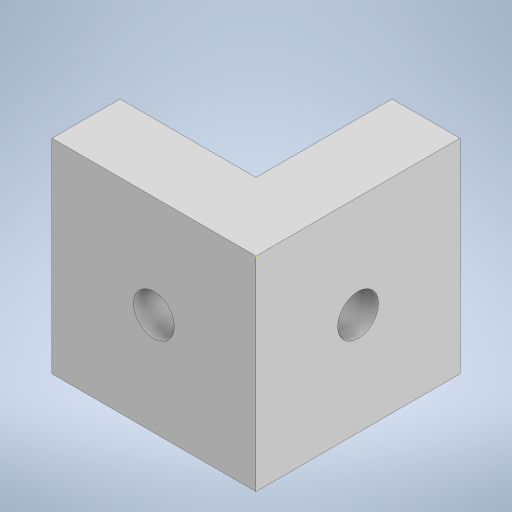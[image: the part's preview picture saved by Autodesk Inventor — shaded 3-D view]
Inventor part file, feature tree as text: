
AUTODESK INVENTOR PART (.ipt)
format: ipt  version: 2023 (Build 270158000, 158)  size: 225,792 bytes
history: native  units: mm
features: sketch x8, extrude x6
ambient origin geometry x8: Origin, YZ Plane, XZ Plane, XY Plane, X Axis, Y Axis, Z Axis, Center Point
bodies: Body1 (feature_tree)
feature tree (14):
  extrude  "Extrusion25"  Depth=30.0mm
  extrude  "Extrusion26"  Depth=30.0mm
  sketch  "Sketch37"  dims[d117=30.0mm d118=10.0mm d119=0.0mm]
  extrude  "Extrusion28"  Depth=10.0mm TaperAngle=0.0deg
  sketch  "Sketch39"  dims[d135=9.0mm d136=5.0mm d137=0.0mm]
  extrude  "Extrusion32"  Depth=10.0mm TaperAngle=0.0deg
  extrude  "Extrusion33"  Depth=5.0mm TaperAngle=0.0deg
  extrude  "Extrusion34"  Depth=5.0mm TaperAngle=0.0deg
  sketch  "Sketch34"  dims[d112=30.0mm d113=30.0mm]
  sketch  "Sketch35"  dims[d114=10.0mm d115=0.0mm d116=30.0mm]
  sketch  "Sketch38"  dims[d123=6.0mm d124=10.0mm d125=0.0mm]
  sketch  "Sketch43"  dims[d138=9.0mm d139=5.0mm d140=0.0mm]
  sketch  "Sketch44"  dims[d141=6.0mm]
  sketch  "Sketch45"  dims[d142=10.0mm d143=0.0mm d49=0.5mm d50=0.872665mm d51=0.5mm d52=0.872665mm d130=0.5mm d131=0.872665mm d132=0.5mm d133=0.872665mm]
